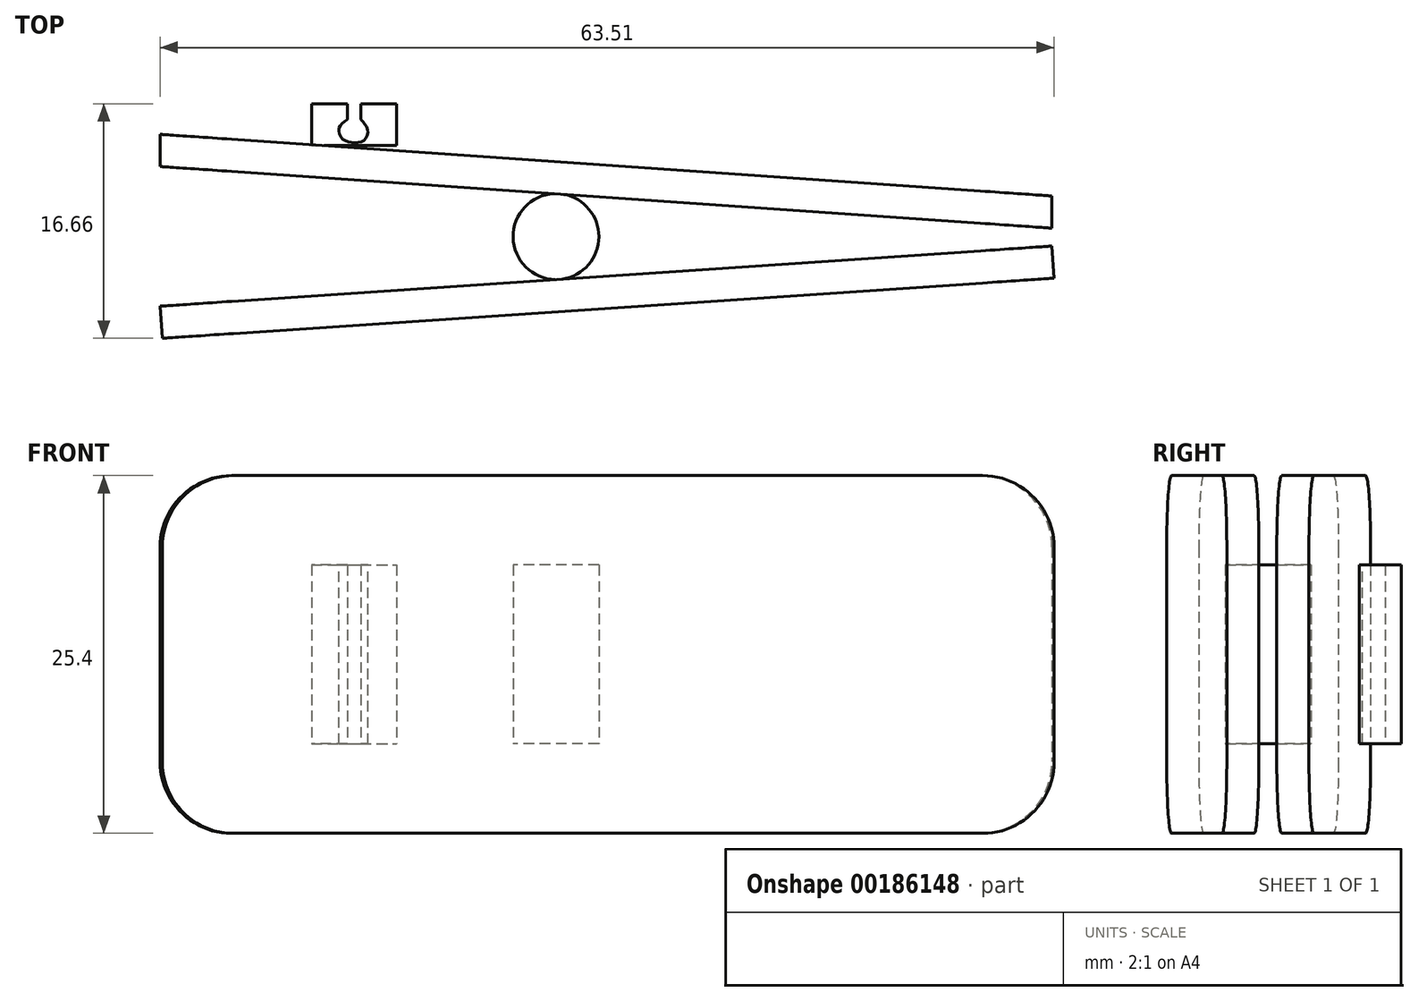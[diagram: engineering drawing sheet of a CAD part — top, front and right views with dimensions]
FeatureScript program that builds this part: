
annotation { "Feature Type Name" : "Feature", "Feature Type Description" : "" }
export const myFeature = defineFeature(function(context is Context, id is Id, definition is map)
    precondition{}
    {
        {
            var Q0;
            Q0=qCreatedBy(makeId("Top.planeOp"),FACE);
            var sketch = newSketch(context, id + "F0", { "sketchPlane" : qUnion([Q0])});
            skLineSegment(sketch, "E0", {"start": v(0, -1.47) * mm, "end": v(-63.36, -5.74) * mm});
            skLineSegment(sketch, "E1", {"start": v(0, -1.47) * mm, "end": v(0.15, -3.75) * mm});
            skLineSegment(sketch, "E2", {"start": v(0.15, -3.75) * mm, "end": v(-63.2, -8.02) * mm});
            skLineSegment(sketch, "E3", {"start": v(-63.2, -8.02) * mm, "end": v(-63.36, -5.74) * mm});
            skLineSegment(sketch, "E4", {"start": v(0, -0.2) * mm, "end": v(-63.35, 4.18) * mm});
            skLineSegment(sketch, "E5", {"start": v(-63.35, 4.18) * mm, "end": v(-63.35, 6.47) * mm});
            skLineSegment(sketch, "E6", {"start": v(-63.35, 6.47) * mm, "end": v(0, 2.09) * mm});
            skLineSegment(sketch, "E7", {"start": v(0, 2.09) * mm, "end": v(0, -0.2) * mm});
            skSolve(sketch);
        }
        {
            var Q0;
            Q0=makeQuery(id+"F0.imprint","IMPRINT",FACE,{"disambiguationData":[TD([[makeQuery(id+"F0.imprint","IMPRINT",EDGE,{"derivedFrom":sQuery(id+"F0.wireOp",EDGE,"E4")}),-1.0]])]});
            var Q1;
            Q1=makeQuery(id+"F0.imprint","IMPRINT",FACE,{"disambiguationData":[TD([[makeQuery(id+"F0.imprint","IMPRINT",EDGE,{"derivedFrom":sQuery(id+"F0.wireOp",EDGE,"E0")}),1.0]])]});
            extrude(context, id + "F1", {"entities" : qUnion([Q0, Q1]), "endBound" : BoundingType.SYMMETRIC, "depth" : 25.4 * mm});
        }
        {
            var Q0;
            Q0=qCreatedBy(makeId("Top.planeOp"),FACE);
            var sketch = newSketch(context, id + "F2", { "sketchPlane" : qUnion([Q0])});
            skCircle(sketch, "E8", {"center": v(-35.23, -0.8) * mm, "radius": 3.05 * mm});
            skLineSegment(sketch, "E9.top", {"start": v(-52.6, 5.66) * mm, "end": v(-46.56, 5.66) * mm});
            skLineSegment(sketch, "E9.left", {"start": v(-52.6, 8.64) * mm, "end": v(-52.6, 5.66) * mm});
            skLineSegment(sketch, "E9.right", {"start": v(-46.56, 8.64) * mm, "end": v(-46.56, 5.66) * mm});
            skLineSegment(sketch, "E10", {"start": v(-49.1, 8.64) * mm, "end": v(-46.56, 8.64) * mm});
            skLineSegment(sketch, "E11", {"start": v(-50.06, 8.64) * mm, "end": v(-52.6, 8.64) * mm});
            skLineSegment(sketch, "E12", {"start": v(-50.06, 8.64) * mm, "end": v(-50.06, 7.52) * mm});
            skLineSegment(sketch, "E13", {"start": v(-49.1, 8.64) * mm, "end": v(-49.1, 7.52) * mm});
            skFitSpline(sketch, "E14", {"points": [v(-50.06, 7.52) * mm, v(-50.62, 6.94) * mm, v(-50.47, 6.21) * mm, v(-49.65, 5.88) * mm, v(-48.83, 6.07) * mm, v(-48.62, 6.82) * mm, v(-49.1, 7.52) * mm], "startDerivative": vector(-4.36, -3.03) * mm, "endDerivative": vector(-3.76, 3.79) * mm});
            skSolve(sketch);
        }
        {
            var Q0;
            Q0=makeQuery(id+"F2.imprint","IMPRINT",FACE,{"disambiguationData":[TD([[makeQuery(id+"F2.imprint","IMPRINT",EDGE,{"derivedFrom":sQuery(id+"F2.wireOp",EDGE,"E8")}),1.0]])]});
            var Q1;
            Q1=makeQuery(id+"F2.imprint","IMPRINT",FACE,{"disambiguationData":[TD([[makeQuery(id+"F2.imprint","IMPRINT",EDGE,{"derivedFrom":sQuery(id+"F2.wireOp",EDGE,"E9.top")}),1.0]])]});
            extrude(context, id + "F3", {"entities" : qUnion([Q0, Q1]), "endBound" : BoundingType.SYMMETRIC, "depth" : 12.7 * mm});
        }
        {
            var Q0;
            Q0=makeQuery(id+"F1.opExtrude","CAP_EDGE",EDGE,{"disambiguationData":[OSD([sQuery(id+"F0.wireOp",EDGE,"E7")])],"isStart":false});
            var Q1;
            Q1=makeQuery(id+"F1.opExtrude","CAP_EDGE",EDGE,{"disambiguationData":[OSD([sQuery(id+"F0.wireOp",EDGE,"E1")])],"isStart":false});
            var Q2;
            Q2=makeQuery(id+"F1.opExtrude","CAP_EDGE",EDGE,{"disambiguationData":[OSD([sQuery(id+"F0.wireOp",EDGE,"E1")])],"isStart":true});
            var Q3;
            Q3=makeQuery(id+"F1.opExtrude","CAP_EDGE",EDGE,{"disambiguationData":[OSD([sQuery(id+"F0.wireOp",EDGE,"E7")])],"isStart":true});
            var Q4;
            Q4=makeQuery(id+"F1.opExtrude","CAP_EDGE",EDGE,{"disambiguationData":[OSD([sQuery(id+"F0.wireOp",EDGE,"E5")])],"isStart":false});
            var Q5;
            Q5=makeQuery(id+"F1.opExtrude","CAP_EDGE",EDGE,{"disambiguationData":[OSD([sQuery(id+"F0.wireOp",EDGE,"E3")])],"isStart":false});
            var Q6;
            Q6=makeQuery(id+"F1.opExtrude","CAP_EDGE",EDGE,{"disambiguationData":[OSD([sQuery(id+"F0.wireOp",EDGE,"E5")])],"isStart":true});
            var Q7;
            Q7=makeQuery(id+"F1.opExtrude","CAP_EDGE",EDGE,{"disambiguationData":[OSD([sQuery(id+"F0.wireOp",EDGE,"E3")])],"isStart":true});
            fillet(context, id + "F4", {"entities" : qUnion([Q0, Q1, Q2, Q3, Q4, Q5, Q6, Q7]), "radius" : 5.08 * mm, "tangentPropagation" : true, "allowEdgeOverflow" : false});
        }
    });
